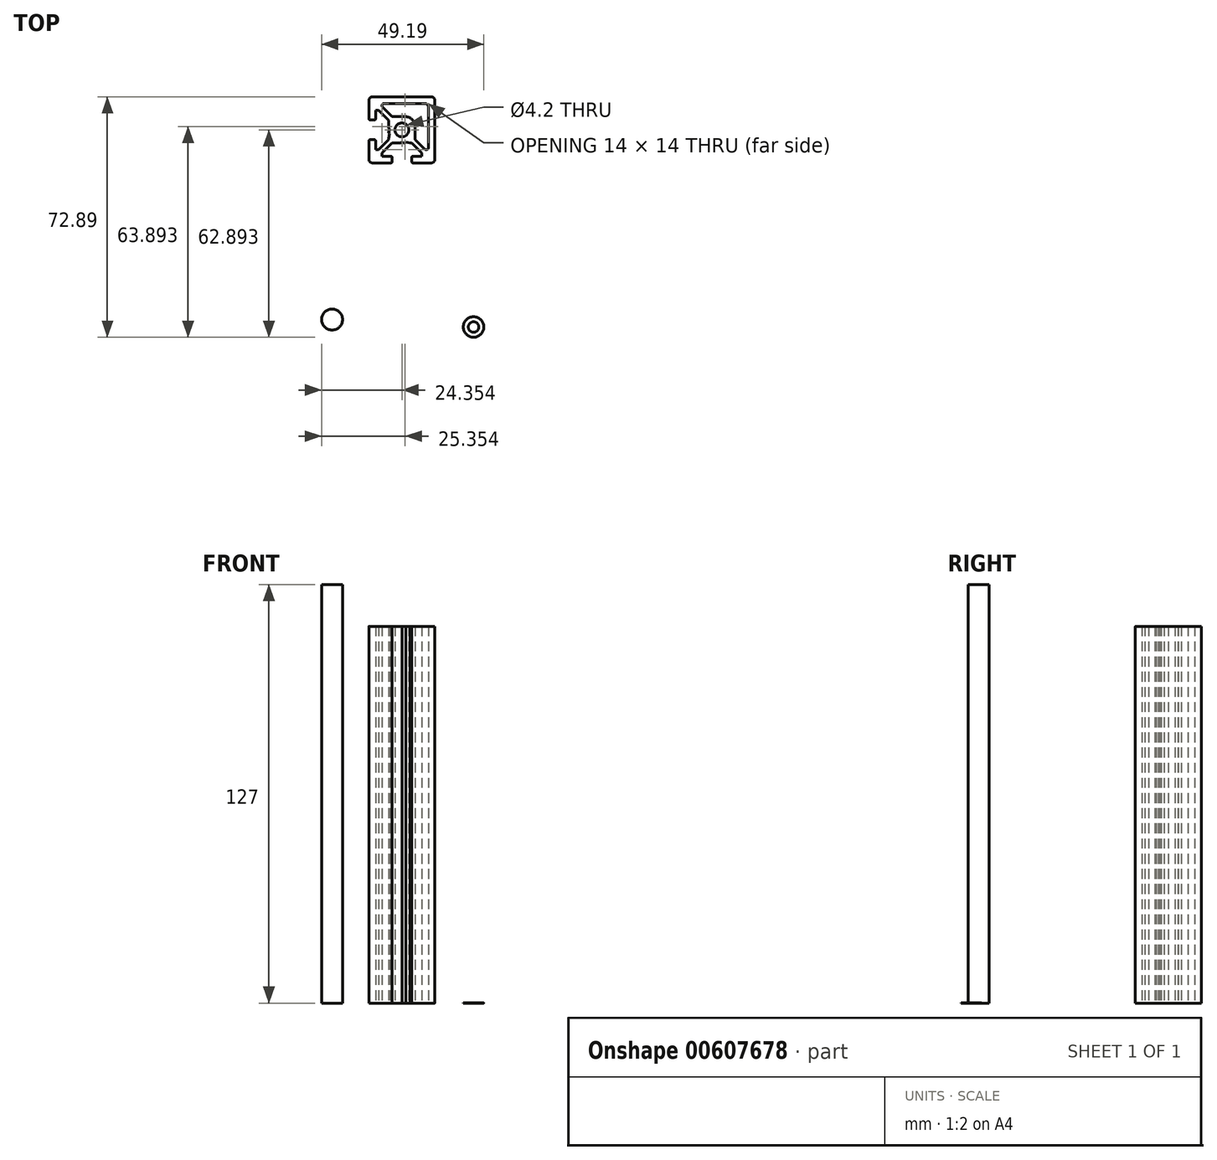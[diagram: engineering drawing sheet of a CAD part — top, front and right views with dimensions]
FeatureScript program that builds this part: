
annotation { "Feature Type Name" : "Feature", "Feature Type Description" : "" }
export const myFeature = defineFeature(function(context is Context, id is Id, definition is map)
    precondition{}
    {
        {
            var Q0;
            Q0=qCreatedBy(makeId("Top.planeOp"),FACE);
            var sketch = newSketch(context, id + "F0", { "sketchPlane" : qUnion([Q0])});
            skCircle(sketch, "E0", {"center": v(-56.04, -48.26) * mm, "radius": 3.18 * mm});
            skCircle(sketch, "E1", {"center": v(-13.12, -50.52) * mm, "radius": 3.1 * mm});
            skCircle(sketch, "E2", {"center": v(-13.12, -50.52) * mm, "radius": 1.6 * mm});
            skSolve(sketch);
        }
        {
            var Q0;
            Q0=makeQuery(id+"F0.imprint","IMPRINT",FACE,{"disambiguationData":[TD([[makeQuery(id+"F0.imprint","IMPRINT",EDGE,{"derivedFrom":sQuery(id+"F0.wireOp",EDGE,"E0")}),1.0]])]});
            extrude(context, id + "F1", {"entities" : qUnion([Q0]), "depth" : 127 * mm, "offsetDistance" : 25 * mm});
        }
        {
            var Q0;
            Q0=qCreatedBy(makeId("Top.planeOp"),FACE);
            var sketch = newSketch(context, id + "F2", { "sketchPlane" : qUnion([Q0])});
            skLineSegment(sketch, "E3", {"start": v(-34.86, 21.27) * mm, "end": v(-34.86, -2.73) * mm});
            skLineSegment(sketch, "E4", {"start": v(-22.86, 9.27) * mm, "end": v(-46.86, 9.27) * mm});
            skLineSegment(sketch, "E5", {"start": v(-25.86, 19.27) * mm, "end": v(-43.86, 19.27) * mm});
            skLineSegment(sketch, "E6", {"start": v(-25.86, -0.73) * mm, "end": v(-31.56, -0.73) * mm});
            skLineSegment(sketch, "E7", {"start": v(-24.86, 18.27) * mm, "end": v(-24.86, 0.27) * mm});
            skLineSegment(sketch, "E8", {"start": v(-44.86, 18.27) * mm, "end": v(-44.86, 12.57) * mm});
            skLineSegment(sketch, "E9", {"start": v(-30.86, 10.27) * mm, "end": v(-30.86, 6.54) * mm});
            skLineSegment(sketch, "E10", {"start": v(-38.86, 12.21) * mm, "end": v(-38.86, 9.93) * mm});
            skLineSegment(sketch, "E11", {"start": v(-33.86, 13.27) * mm, "end": v(-37.59, 13.27) * mm});
            skLineSegment(sketch, "E12", {"start": v(-27.86, 17.27) * mm, "end": v(-40.36, 17.27) * mm});
            skLineSegment(sketch, "E13", {"start": v(-26.86, 16.27) * mm, "end": v(-26.86, 3.77) * mm});
            skLineSegment(sketch, "E14", {"start": v(-42.86, 15.27) * mm, "end": v(-42.86, 12.57) * mm});
            skLineSegment(sketch, "E15", {"start": v(-43.16, 12.27) * mm, "end": v(-44.56, 12.27) * mm});
            skLineSegment(sketch, "E16", {"start": v(-43.16, 6.27) * mm, "end": v(-44.56, 6.27) * mm});
            skLineSegment(sketch, "E17", {"start": v(-41.92, 3.27) * mm, "end": v(-42.86, 3.27) * mm});
            skLineSegment(sketch, "E18", {"start": v(-42.86, 5.97) * mm, "end": v(-42.86, 3.27) * mm});
            skLineSegment(sketch, "E19", {"start": v(-44.86, 5.97) * mm, "end": v(-44.86, 0.27) * mm});
            skLineSegment(sketch, "E20", {"start": v(-41.92, 15.27) * mm, "end": v(-42.86, 15.27) * mm});
            skLineSegment(sketch, "E21", {"start": v(-38.79, 8.87) * mm, "end": v(-38.56, 9.27) * mm});
            skLineSegment(sketch, "E22", {"start": v(-38.79, 9.68) * mm, "end": v(-38.56, 9.27) * mm});
            skLineSegment(sketch, "E23", {"start": v(-38.86, 6.77) * mm, "end": v(-38.86, 6.33) * mm});
            skLineSegment(sketch, "E24", {"start": v(-38.86, 12.21) * mm, "end": v(-41.92, 15.27) * mm});
            skLineSegment(sketch, "E25", {"start": v(-38.86, 6.33) * mm, "end": v(-41.92, 3.27) * mm});
            skLineSegment(sketch, "E26", {"start": v(-38.86, 6.77) * mm, "end": v(-38.6, 8.05) * mm});
            skArc(sketch, "E27", {"start": v(-38.79, 8.87) * mm, "mid": v(-38.86, 8.62) * mm, "end": v(-38.79, 8.37) * mm});
            skLineSegment(sketch, "E28", {"start": v(-38.79, 8.37) * mm, "end": v(-38.6, 8.05) * mm});
            skArc(sketch, "E29", {"start": v(-38.86, 9.93) * mm, "mid": v(-38.84, 9.8) * mm, "end": v(-38.79, 9.68) * mm});
            skArc(sketch, "E30", {"start": v(-43.16, 12.27) * mm, "mid": v(-42.94, 12.36) * mm, "end": v(-42.86, 12.57) * mm});
            skArc(sketch, "E31", {"start": v(-44.86, 12.57) * mm, "mid": v(-44.77, 12.36) * mm, "end": v(-44.56, 12.27) * mm});
            skArc(sketch, "E32", {"start": v(-42.86, 5.97) * mm, "mid": v(-42.94, 6.19) * mm, "end": v(-43.16, 6.27) * mm});
            skArc(sketch, "E33", {"start": v(-44.56, 6.27) * mm, "mid": v(-44.77, 6.19) * mm, "end": v(-44.86, 5.97) * mm});
            skLineSegment(sketch, "E34", {"start": v(-37.8, 5.27) * mm, "end": v(-35.51, 5.27) * mm});
            skLineSegment(sketch, "E35", {"start": v(-32.36, 5.27) * mm, "end": v(-31.92, 5.27) * mm});
            skArc(sketch, "E36", {"start": v(-38.16, -0.73) * mm, "mid": v(-37.94, -0.64) * mm, "end": v(-37.86, -0.43) * mm});
            skLineSegment(sketch, "E37", {"start": v(-40.86, 1.27) * mm, "end": v(-38.16, 1.27) * mm});
            skArc(sketch, "E38", {"start": v(-37.86, 0.97) * mm, "mid": v(-37.94, 1.19) * mm, "end": v(-38.16, 1.27) * mm});
            skLineSegment(sketch, "E39", {"start": v(-31.56, 1.27) * mm, "end": v(-28.86, 1.27) * mm});
            skArc(sketch, "E40", {"start": v(-31.56, 1.27) * mm, "mid": v(-31.77, 1.19) * mm, "end": v(-31.86, 0.97) * mm});
            skLineSegment(sketch, "E41", {"start": v(-28.86, 2.21) * mm, "end": v(-28.86, 1.27) * mm});
            skLineSegment(sketch, "E42", {"start": v(-40.86, 2.21) * mm, "end": v(-40.86, 1.27) * mm});
            skLineSegment(sketch, "E43", {"start": v(-31.86, 0.97) * mm, "end": v(-31.86, -0.43) * mm});
            skArc(sketch, "E44", {"start": v(-31.86, -0.43) * mm, "mid": v(-31.77, -0.64) * mm, "end": v(-31.56, -0.73) * mm});
            skLineSegment(sketch, "E45", {"start": v(-37.86, 0.97) * mm, "end": v(-37.86, -0.43) * mm});
            skLineSegment(sketch, "E46", {"start": v(-34.45, 5.34) * mm, "end": v(-34.86, 5.57) * mm});
            skLineSegment(sketch, "E47", {"start": v(-35.26, 5.34) * mm, "end": v(-34.86, 5.57) * mm});
            skArc(sketch, "E48", {"start": v(-35.51, 5.27) * mm, "mid": v(-35.38, 5.3) * mm, "end": v(-35.26, 5.34) * mm});
            skLineSegment(sketch, "E49", {"start": v(-31.92, 5.27) * mm, "end": v(-28.86, 2.21) * mm});
            skLineSegment(sketch, "E50", {"start": v(-37.8, 5.27) * mm, "end": v(-40.86, 2.21) * mm});
            skLineSegment(sketch, "E51", {"start": v(-32.36, 5.27) * mm, "end": v(-33.64, 5.52) * mm});
            skArc(sketch, "E52", {"start": v(-34.45, 5.34) * mm, "mid": v(-34.2, 5.27) * mm, "end": v(-33.95, 5.34) * mm});
            skLineSegment(sketch, "E53", {"start": v(-33.95, 5.34) * mm, "end": v(-33.64, 5.52) * mm});
            skLineSegment(sketch, "E54", {"start": v(-38.16, -0.73) * mm, "end": v(-43.86, -0.73) * mm});
            skLineSegment(sketch, "E55", {"start": v(-30.7, 6.19) * mm, "end": v(-27.94, 3.42) * mm});
            skLineSegment(sketch, "E56", {"start": v(-37.94, 13.42) * mm, "end": v(-40.7, 16.19) * mm});
            skLineSegment(sketch, "E57", {"start": v(-40.86, 16.77) * mm, "end": v(-40.86, 16.54) * mm});
            skLineSegment(sketch, "E58", {"start": v(-27.36, 3.27) * mm, "end": v(-27.59, 3.27) * mm});
            skCircle(sketch, "E59", {"center": v(-34.86, 9.27) * mm, "radius": 2.1 * mm});
            skArc(sketch, "E60", {"start": v(-26.86, 16.27) * mm, "mid": v(-27.15, 16.98) * mm, "end": v(-27.86, 17.27) * mm});
            skArc(sketch, "E61", {"start": v(-24.86, 18.27) * mm, "mid": v(-25.15, 18.98) * mm, "end": v(-25.86, 19.27) * mm});
            skArc(sketch, "E62", {"start": v(-25.86, -0.73) * mm, "mid": v(-25.15, -0.43) * mm, "end": v(-24.86, 0.27) * mm});
            skArc(sketch, "E63", {"start": v(-44.86, 0.27) * mm, "mid": v(-44.56, -0.43) * mm, "end": v(-43.86, -0.73) * mm});
            skArc(sketch, "E64", {"start": v(-43.86, 19.27) * mm, "mid": v(-44.56, 18.98) * mm, "end": v(-44.86, 18.27) * mm});
            skArc(sketch, "E65", {"start": v(-27.36, 3.27) * mm, "mid": v(-27, 3.42) * mm, "end": v(-26.86, 3.77) * mm});
            skArc(sketch, "E66", {"start": v(-27.94, 3.42) * mm, "mid": v(-27.78, 3.31) * mm, "end": v(-27.59, 3.27) * mm});
            skArc(sketch, "E67", {"start": v(-40.36, 17.27) * mm, "mid": v(-40.7, 17.13) * mm, "end": v(-40.86, 16.77) * mm});
            skArc(sketch, "E68", {"start": v(-40.86, 16.54) * mm, "mid": v(-40.82, 16.35) * mm, "end": v(-40.7, 16.19) * mm});
            skArc(sketch, "E69", {"start": v(-37.94, 13.42) * mm, "mid": v(-37.78, 13.31) * mm, "end": v(-37.59, 13.27) * mm});
            skArc(sketch, "E70", {"start": v(-30.86, 6.54) * mm, "mid": v(-30.82, 6.35) * mm, "end": v(-30.7, 6.19) * mm});
            skArc(sketch, "E71", {"start": v(-30.86, 10.27) * mm, "mid": v(-31.74, 12.4) * mm, "end": v(-33.86, 13.27) * mm});
            skLineSegment(sketch, "E72", {"start": v(48.08, 19.27) * mm, "end": v(-1.92, 19.27) * mm});
            skLineSegment(sketch, "E73", {"start": v(48.08, -0.73) * mm, "end": v(-1.92, -0.73) * mm});
            skLineSegment(sketch, "E74", {"start": v(50.08, 9.27) * mm, "end": v(-3.92, 9.27) * mm});
            skLineSegment(sketch, "E75", {"start": v(-1.92, 19.27) * mm, "end": v(-1.92, -0.73) * mm});
            skLineSegment(sketch, "E76", {"start": v(48.08, 19.27) * mm, "end": v(48.08, -0.73) * mm});
            skSolve(sketch);
        }
        {
            var Q0;
            Q0=makeQuery(id+"F2.imprint","IMPRINT",FACE,{"disambiguationData":[TD([[makeQuery(id+"F2.imprint","IMPRINT",EDGE,{"derivedFrom":sQuery(id+"F2.wireOp",EDGE,"E8")}),1.0]])]});
            var Q1;
            {var subQ4=sQuery(id+"F2.wireOp",EDGE,"E60");Q1=makeQuery(id+"F2.imprint","IMPRINT",FACE,{"disambiguationData":[TD([[makeQuery(id+"F2.imprint","IMPRINT",EDGE,{"derivedFrom":subQ4}),-1.0]])]});}
            var Q2;
            Q2=makeQuery(id+"F2.imprint","IMPRINT",FACE,{"disambiguationData":[TD([[makeQuery(id+"F2.imprint","IMPRINT",EDGE,{"derivedFrom":sQuery(id+"F2.wireOp",EDGE,"E6")}),-1.0]])]});
            var Q3;
            {var subQ0=sQuery(id+"F2.wireOp",EDGE,"E71");Q3=makeQuery(id+"F2.imprint","IMPRINT",FACE,{"disambiguationData":[TD([[makeQuery(id+"F2.imprint","IMPRINT",EDGE,{"derivedFrom":subQ0}),1.0]])]});}
            var Q4;
            Q4=makeQuery(id+"F2.imprint","IMPRINT",FACE,{"disambiguationData":[TD([[makeQuery(id+"F2.imprint","IMPRINT",EDGE,{"derivedFrom":sQuery(id+"F2.wireOp",EDGE,"E16")}),1.0]])]});
            extrude(context, id + "F3", {"entities" : qUnion([Q0, Q1, Q2, Q3, Q4]), "depth" : 114.3 * mm, "offsetDistance" : 25 * mm});
        }
        {
            var Q0;
            Q0=makeQuery(id+"F0.imprint","IMPRINT",FACE,{"disambiguationData":[TD([[makeQuery(id+"F0.imprint","IMPRINT",EDGE,{"derivedFrom":sQuery(id+"F0.wireOp",EDGE,"E1")}),1.0]])]});
            extrude(context, id + "F4", {"entities" : qUnion([Q0]), "depth" : 11 / 406.4 * mm, "offsetDistance" : 25 * mm});
        }
    });
